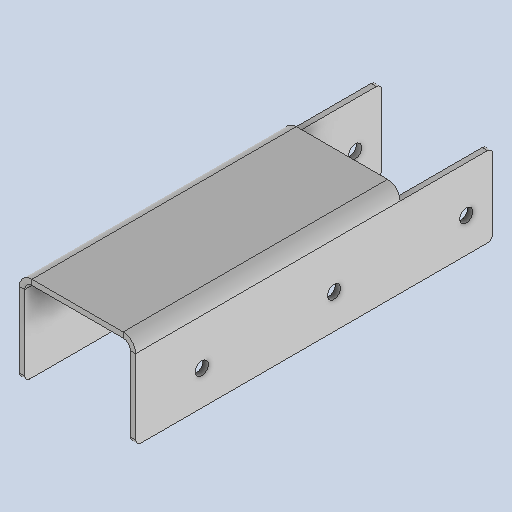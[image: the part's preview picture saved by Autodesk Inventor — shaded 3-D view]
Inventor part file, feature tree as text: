
AUTODESK INVENTOR PART (.ipt)
format: ipt  version: 2025 (Build 290162010, 162A)  size: 211,456 bytes
history: native  units: mm
features: sheet_metal_op x4, sketch x4, other x3, extrude x2, projected_geometry x2, pattern_linear x1, fillet x1
ambient origin geometry x8: Origin, YZ Plane, XZ Plane, XY Plane, X Axis, Y Axis, Z Axis, Center Point
bodies: Solid1 (feature_tree)
feature tree (17):
  sheet_metal_op  "Face1"
  sheet_metal_op  "Flange1"
  sketch  "Sketch5"  dims[d5=4.0mm d6=2.75mm d7=35.0mm d8=90.0deg d9=2.75mm d10=8.0mm d11=2.0mm d12=2.75mm d14=0.0mm d15=13.0mm d17=2.5mm d18=25.0mm d19=0.0mm d20=0.0mm d21=30.0mm d23=50.0mm d24=35.0mm d25=0.0mm d26=2.0mm]
  extrude  "Extrusion2"  Depth=100.0mm
  extrude  "Extrusion1"  Depth=2.0mm
  pattern_linear  "Rectangular Pattern1"  Spacing1=2.75mm  [1 undecoded]
  fillet  "Fillet1"  Radius=35.0mm
  sketch  "Sketch1"  dims[d0=40.0mm d1=100.0mm]
  other  "Plate1"
  sketch  "Sketch2"  dims[d2=2.0mm d3=2.0mm]
  other  "Plate2"
  sheet_metal_op  "Bend1"
  sheet_metal_op  "Corner1"
  sketch  "Sketch3"  dims[d4=1.0mm]
  projected_geometry  "Projected Loop1"
  projected_geometry  "Projected Loop2"
  other  "Definition1"
note: 1 required parameter value undecoded (feature->parameter linkage not recoverable at this tier; creation-order binding heuristic only, values carry confidence <= 0.55)
